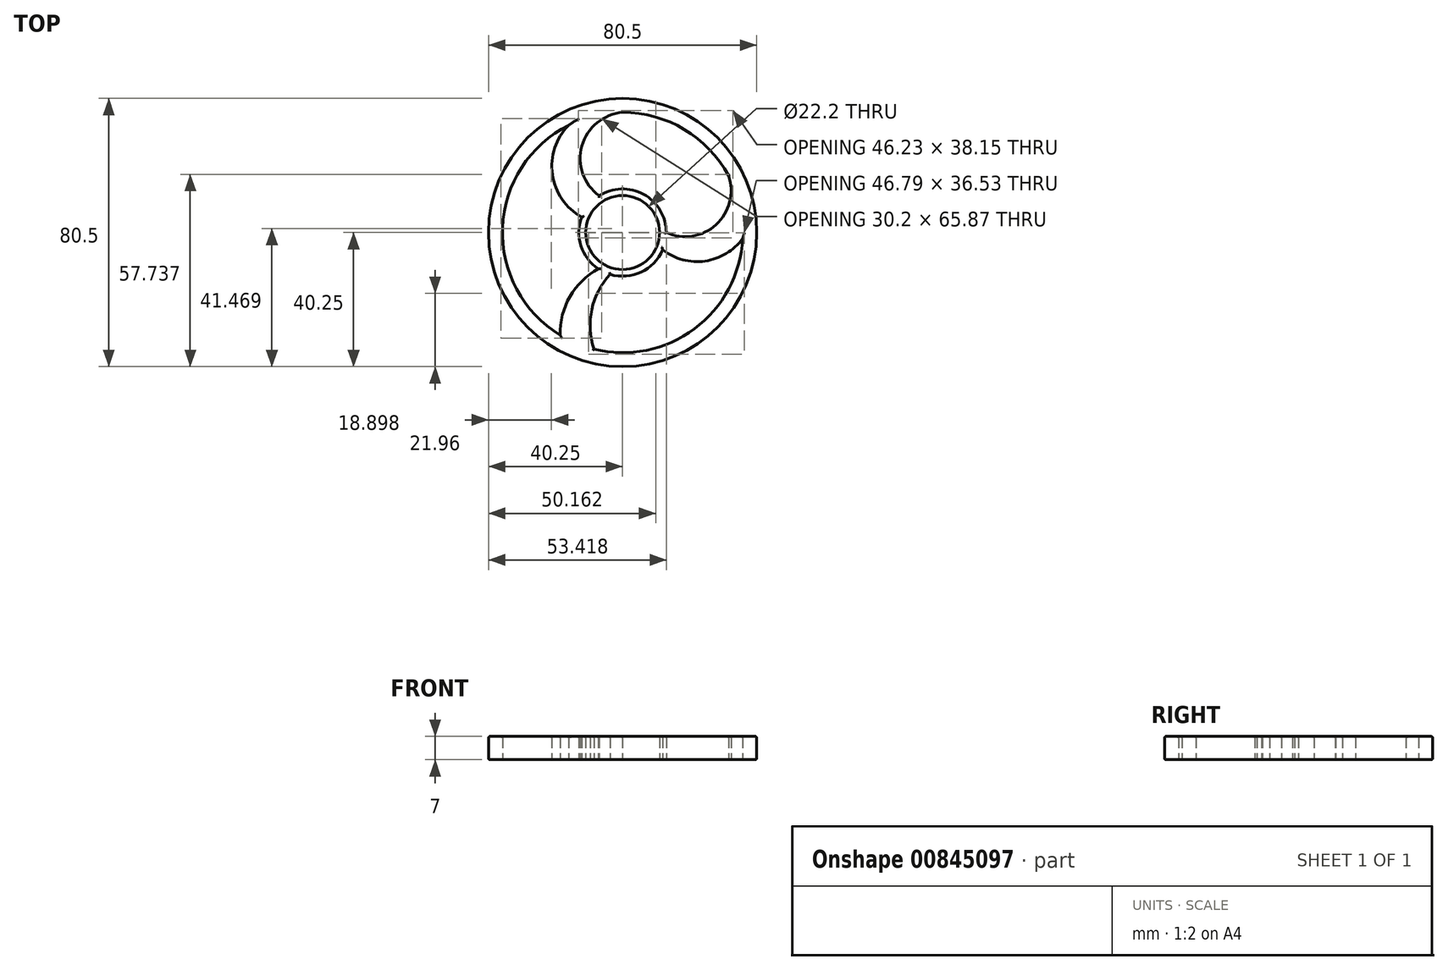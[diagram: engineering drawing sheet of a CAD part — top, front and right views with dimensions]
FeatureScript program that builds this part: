
annotation { "Feature Type Name" : "Feature", "Feature Type Description" : "" }
export const myFeature = defineFeature(function(context is Context, id is Id, definition is map)
    precondition{}
    {
        {
            var Q0;
            Q0=qCreatedBy(makeId("Top.planeOp"),FACE);
            var sketch = newSketch(context, id + "F0", { "sketchPlane" : qUnion([Q0])});
            skCircle(sketch, "E0", {"center": v(0, 0) * mm, "radius": 40.25 * mm});
            skArc(sketch, "E1", {"start": v(-16.2, 32.22) * mm, "mid": v(-36.03, 1.45) * mm, "end": v(-18.74, -30.81) * mm});
            skCircle(sketch, "E2", {"center": v(0, 0) * mm, "radius": 11.1 * mm});
            skArc(sketch, "E3", {"start": v(-3.75, -12.55) * mm, "mid": v(5.53, -11.88) * mm, "end": v(12.02, -5.2) * mm});
            skArc(sketch, "E4", {"start": v(-16.2, 32.22) * mm, "mid": v(-21.07, 17.45) * mm, "end": v(-12.25, 4.65) * mm});
            skArc(sketch, "E5", {"start": v(0, 36.06) * mm, "mid": v(-12.2, 26) * mm, "end": v(-7.05, 11.04) * mm});
            skArc(sketch, "E6", {"start": v(13.1, 0) * mm, "mid": v(28.06, 2.37) * mm, "end": v(31.78, 17.05) * mm});
            skArc(sketch, "E7", {"start": v(12.02, -5.2) * mm, "mid": v(24.74, -8.56) * mm, "end": v(36.02, -1.78) * mm});
            skArc(sketch, "E8", {"start": v(-3.75, -12.55) * mm, "mid": v(-9.25, -23.12) * mm, "end": v(-8.62, -35.02) * mm});
            skArc(sketch, "E9", {"start": v(-7.27, -10.9) * mm, "mid": v(-15.82, -19.23) * mm, "end": v(-18.74, -30.81) * mm});
            skArc(sketch, "E10.trimOffspring", {"start": v(31.78, 17.05) * mm, "mid": v(18.52, 30.95) * mm, "end": v(0, 36.06) * mm});
            skArc(sketch, "E11.trimOffspring", {"start": v(-8.62, -35.02) * mm, "mid": v(21.54, -28.92) * mm, "end": v(36.02, -1.78) * mm});
            skArc(sketch, "E12.trimOffspring", {"start": v(13.1, 0) * mm, "mid": v(6.3, 11.49) * mm, "end": v(-7.05, 11.04) * mm});
            skArc(sketch, "E13.trimOffspring", {"start": v(-12.25, 4.65) * mm, "mid": v(-12.48, -4) * mm, "end": v(-7.27, -10.9) * mm});
            skSolve(sketch);
        }
        {
            var Q0;
            Q0=qSketchRegion(id+"F0",true);
            extrude(context, id + "F1", {"entities" : qUnion([Q0]), "depth" : 7 * mm, "offsetDistance" : 25 * mm});
        }
        {
            var Q0;
            Q0=makeQuery(id+"F1.opExtrude","CAP_EDGE",EDGE,{"disambiguationData":[OSD([sQuery(id+"F0.wireOp",EDGE,"E0")])],"isStart":false});
            var Q1;
            Q1=makeQuery(id+"F1.opExtrude","CAP_EDGE",EDGE,{"disambiguationData":[OSD([sQuery(id+"F0.wireOp",EDGE,"E1")])],"isStart":false});
            var Q2;
            Q2=makeQuery(id+"F1.opExtrude","CAP_EDGE",EDGE,{"disambiguationData":[OSD([sQuery(id+"F0.wireOp",EDGE,"E9")])],"isStart":false});
            var Q3;
            Q3=makeQuery(id+"F1.opExtrude","CAP_EDGE",EDGE,{"disambiguationData":[OSD([sQuery(id+"F0.wireOp",EDGE,"E7")])],"isStart":false});
            var Q4;
            Q4=makeQuery(id+"F1.opExtrude","CAP_EDGE",EDGE,{"disambiguationData":[OSD([sQuery(id+"F0.wireOp",EDGE,"E8")])],"isStart":false});
            var Q5;
            Q5=makeQuery(id+"F1.opExtrude","CAP_EDGE",EDGE,{"disambiguationData":[OSD([sQuery(id+"F0.wireOp",EDGE,"E3")])],"isStart":false});
            var Q6;
            Q6=makeQuery(id+"F1.opExtrude","CAP_EDGE",EDGE,{"disambiguationData":[OSD([sQuery(id+"F0.wireOp",EDGE,"E8")])],"isStart":true});
            var Q7;
            Q7=makeQuery(id+"F1.opExtrude","CAP_EDGE",EDGE,{"disambiguationData":[OSD([sQuery(id+"F0.wireOp",EDGE,"E3")])],"isStart":true});
            var Q8;
            Q8=makeQuery(id+"F1.opExtrude","CAP_EDGE",EDGE,{"disambiguationData":[OSD([sQuery(id+"F0.wireOp",EDGE,"E11.trimOffspring")])],"isStart":false});
            var Q9;
            Q9=makeQuery(id+"F1.opExtrude","CAP_EDGE",EDGE,{"disambiguationData":[OSD([sQuery(id+"F0.wireOp",EDGE,"E6")])],"isStart":false});
            var Q10;
            Q10=makeQuery(id+"F1.opExtrude","CAP_EDGE",EDGE,{"disambiguationData":[OSD([sQuery(id+"F0.wireOp",EDGE,"E10.trimOffspring")])],"isStart":false});
            var Q11;
            Q11=makeQuery(id+"F1.opExtrude","CAP_EDGE",EDGE,{"disambiguationData":[OSD([sQuery(id+"F0.wireOp",EDGE,"E5")])],"isStart":false});
            var Q12;
            Q12=makeQuery(id+"F1.opExtrude","CAP_EDGE",EDGE,{"disambiguationData":[OSD([sQuery(id+"F0.wireOp",EDGE,"E4")])],"isStart":false});
            var Q13;
            Q13=makeQuery(id+"F1.opExtrude","CAP_EDGE",EDGE,{"disambiguationData":[OSD([sQuery(id+"F0.wireOp",EDGE,"E0")])],"isStart":true});
            var Q14;
            Q14=makeQuery(id+"F1.opExtrude","CAP_EDGE",EDGE,{"disambiguationData":[OSD([sQuery(id+"F0.wireOp",EDGE,"E11.trimOffspring")])],"isStart":true});
            var Q15;
            Q15=makeQuery(id+"F1.opExtrude","CAP_EDGE",EDGE,{"disambiguationData":[OSD([sQuery(id+"F0.wireOp",EDGE,"E7")])],"isStart":true});
            var Q16;
            Q16=makeQuery(id+"F1.opExtrude","CAP_EDGE",EDGE,{"disambiguationData":[OSD([sQuery(id+"F0.wireOp",EDGE,"E2")])],"isStart":true});
            var Q17;
            Q17=makeQuery(id+"F1.opExtrude","CAP_EDGE",EDGE,{"disambiguationData":[OSD([sQuery(id+"F0.wireOp",EDGE,"E9")])],"isStart":true});
            var Q18;
            Q18=makeQuery(id+"F1.opExtrude","CAP_EDGE",EDGE,{"disambiguationData":[OSD([sQuery(id+"F0.wireOp",EDGE,"E4")])],"isStart":true});
            var Q19;
            Q19=makeQuery(id+"F1.opExtrude","CAP_EDGE",EDGE,{"disambiguationData":[OSD([sQuery(id+"F0.wireOp",EDGE,"E12.trimOffspring")])],"isStart":true});
            var Q20;
            Q20=makeQuery(id+"F1.opExtrude","CAP_EDGE",EDGE,{"disambiguationData":[OSD([sQuery(id+"F0.wireOp",EDGE,"E13.trimOffspring")])],"isStart":true});
            var Q21;
            Q21=makeQuery(id+"F1.opExtrude","CAP_EDGE",EDGE,{"disambiguationData":[OSD([sQuery(id+"F0.wireOp",EDGE,"E1")])],"isStart":true});
            var Q22;
            Q22=makeQuery(id+"F1.opExtrude","CAP_EDGE",EDGE,{"disambiguationData":[OSD([sQuery(id+"F0.wireOp",EDGE,"E5")])],"isStart":true});
            var Q23;
            Q23=makeQuery(id+"F1.opExtrude","CAP_EDGE",EDGE,{"disambiguationData":[OSD([sQuery(id+"F0.wireOp",EDGE,"E10.trimOffspring")])],"isStart":true});
            var Q24;
            Q24=makeQuery(id+"F1.opExtrude","CAP_EDGE",EDGE,{"disambiguationData":[OSD([sQuery(id+"F0.wireOp",EDGE,"E6")])],"isStart":true});
            var Q25;
            Q25=makeQuery(id+"F1.opExtrude","CAP_EDGE",EDGE,{"disambiguationData":[OSD([sQuery(id+"F0.wireOp",EDGE,"E13.trimOffspring")])],"isStart":false});
            var Q26;
            Q26=makeQuery(id+"F1.opExtrude","CAP_EDGE",EDGE,{"disambiguationData":[OSD([sQuery(id+"F0.wireOp",EDGE,"E2")])],"isStart":false});
            var Q27;
            Q27=makeQuery(id+"F1.opExtrude","CAP_EDGE",EDGE,{"disambiguationData":[OSD([sQuery(id+"F0.wireOp",EDGE,"E12.trimOffspring")])],"isStart":false});
            fillet(context, id + "F2", {"entities" : qUnion([Q0, Q1, Q2, Q3, Q4, Q5, Q6, Q7, Q8, Q9, Q10, Q11, Q12, Q13, Q14, Q15, Q16, Q17, Q18, Q19, Q20, Q21, Q22, Q23, Q24, Q25, Q26, Q27]), "radius" : .5 * mm, "tangentPropagation" : true, "allowEdgeOverflow" : false});
        }
    });
